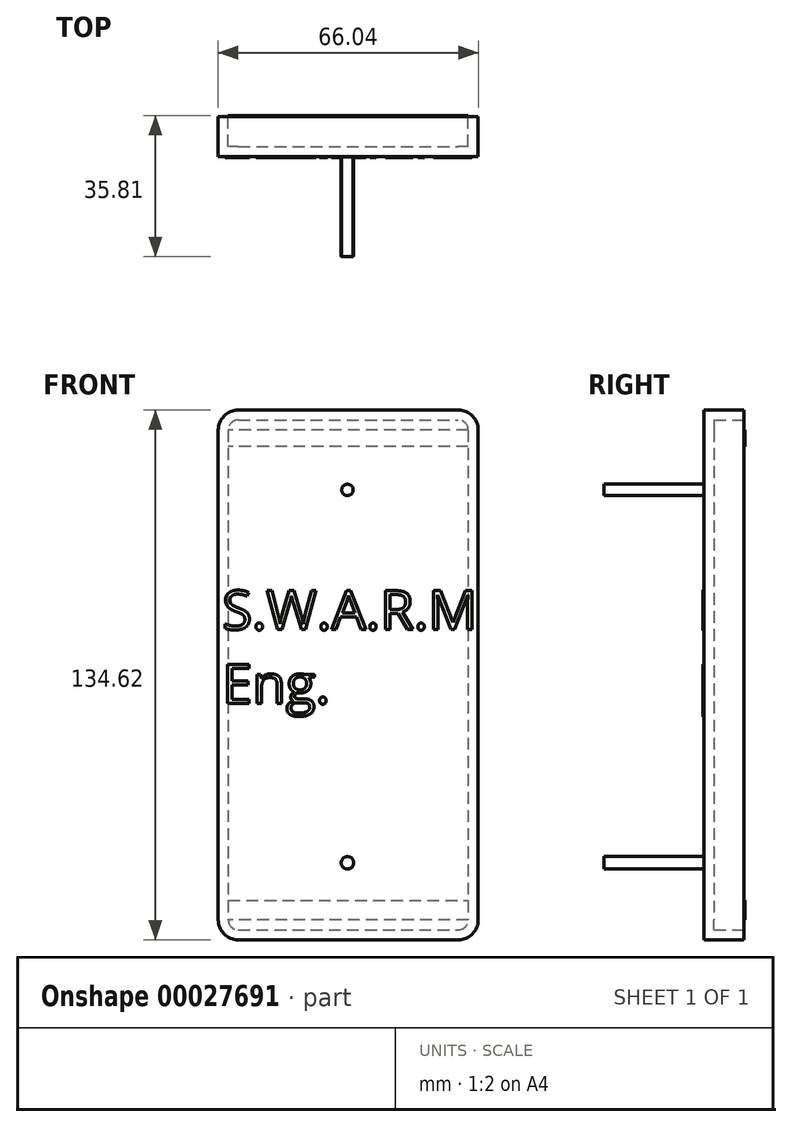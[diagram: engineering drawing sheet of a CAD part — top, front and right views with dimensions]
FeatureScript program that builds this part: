
annotation { "Feature Type Name" : "Feature", "Feature Type Description" : "" }
export const myFeature = defineFeature(function(context is Context, id is Id, definition is map)
    precondition{}
    {
        {
            var Q0;
            Q0=qCreatedBy(makeId("Front.planeOp"),FACE);
            var sketch = newSketch(context, id + "F0", { "sketchPlane" : qUnion([Q0])});
            skLineSegment(sketch, "E0.bottom", {"start": v(-32.82, 79.31) * mm, "end": v(33.22, 79.31) * mm});
            skLineSegment(sketch, "E0.top", {"start": v(-32.82, -55.3) * mm, "end": v(33.22, -55.3) * mm});
            skLineSegment(sketch, "E0.left", {"start": v(-32.82, 79.31) * mm, "end": v(-32.82, -55.3) * mm});
            skLineSegment(sketch, "E0.right", {"start": v(33.22, 79.31) * mm, "end": v(33.22, -55.3) * mm});
            skSolve(sketch);
        }
        {
            var Q0;
            Q0 = qSketchRegion(id + "F0", true);
            extrude(context, id + "F1", {"entities" : qUnion([Q0]), "depth" : 10.16 * mm});
        }
        {
            var Q0;
            Q0=makeQuery(id+"F1.opExtrude","SWEPT_EDGE",EDGE,{"disambiguationData":[OSD([sQuery(id+"F0.wireOp",EDGE,"E0.bottom"),sQuery(id+"F0.wireOp",EDGE,"E0.left")])]});
            var Q1;
            Q1=makeQuery(id+"F1.opExtrude","SWEPT_EDGE",EDGE,{"disambiguationData":[OSD([sQuery(id+"F0.wireOp",EDGE,"E0.bottom"),sQuery(id+"F0.wireOp",EDGE,"E0.right")])]});
            var Q2;
            Q2=makeQuery(id+"F1.opExtrude","SWEPT_EDGE",EDGE,{"disambiguationData":[OSD([sQuery(id+"F0.wireOp",EDGE,"E0.top"),sQuery(id+"F0.wireOp",EDGE,"E0.right")])]});
            var Q3;
            Q3=makeQuery(id+"F1.opExtrude","SWEPT_EDGE",EDGE,{"disambiguationData":[OSD([sQuery(id+"F0.wireOp",EDGE,"E0.top"),sQuery(id+"F0.wireOp",EDGE,"E0.left")])]});
            fillet(context, id + "F2", {"entities" : qUnion([Q0, Q1, Q2, Q3]), "radius" : 5.08 * mm, "tangentPropagation" : true, "allowEdgeOverflow" : false});
        }
        {
            var Q0;
            Q0=makeQuery(id+"F1.opExtrude","CAP_FACE",FACE,{"disambiguationData":[OSD([sQuery(id+"F0.wireOp",EDGE,"E0.bottom"),sQuery(id+"F0.wireOp",EDGE,"E0.top"),sQuery(id+"F0.wireOp",EDGE,"E0.left"),sQuery(id+"F0.wireOp",EDGE,"E0.right")])],"isStart":true});
            shell(context, id + "F3", {"entities" : qUnion([Q0]), "thickness" : 2.54 * mm});
        }
        {
            var Q0;
            Q0=makeQuery(id+"F1.opExtrude","CAP_FACE",FACE,{"disambiguationData":[OSD([sQuery(id+"F0.wireOp",EDGE,"E0.bottom"),sQuery(id+"F0.wireOp",EDGE,"E0.top"),sQuery(id+"F0.wireOp",EDGE,"E0.left"),sQuery(id+"F0.wireOp",EDGE,"E0.right")])],"isStart":true});
            var sketch = newSketch(context, id + "F4", { "sketchPlane" : qUnion([Q0])});
            skLineSegment(sketch, "E1", {"start": v(-30.68, 74.23) * mm, "end": v(30.28, 74.23) * mm});
            skLineSegment(sketch, "E2", {"start": v(-30.68, 74.23) * mm, "end": v(-30.68, 70) * mm});
            skLineSegment(sketch, "E3", {"start": v(-30.68, 70) * mm, "end": v(30.28, 70) * mm});
            skLineSegment(sketch, "E4", {"start": v(30.28, 70) * mm, "end": v(30.28, 74.23) * mm});
            skLineSegment(sketch, "E5", {"start": v(-30.68, -50.23) * mm, "end": v(30.28, -50.23) * mm});
            skLineSegment(sketch, "E6", {"start": v(30.28, -50.23) * mm, "end": v(30.28, -45.31) * mm});
            skLineSegment(sketch, "E7", {"start": v(30.28, -45.31) * mm, "end": v(-30.68, -45.31) * mm});
            skLineSegment(sketch, "E8", {"start": v(-30.68, -45.31) * mm, "end": v(-30.68, -50.23) * mm});
            skSolve(sketch);
        }
        {
            var Q0;
            Q0 = qSketchRegion(id + "F4", true);
            extrude(context, id + "F5", {"entities" : qUnion([Q0]), "depth" : 0.25 * mm});
        }
        {
            var Q0;
            Q0=makeQuery(id+"F1.opExtrude","CAP_FACE",FACE,{"disambiguationData":[OSD([sQuery(id+"F0.wireOp",EDGE,"E0.bottom"),sQuery(id+"F0.wireOp",EDGE,"E0.top"),sQuery(id+"F0.wireOp",EDGE,"E0.left"),sQuery(id+"F0.wireOp",EDGE,"E0.right")])],"isStart":false});
            var sketch = newSketch(context, id + "F6", { "sketchPlane" : qUnion([Q0])});
            skCircle(sketch, "E9", {"center": v(0, 59.02) * mm, "radius": 1.47 * mm});
            skCircle(sketch, "E10", {"center": v(0, -35.72) * mm, "radius": 1.59 * mm});
            skSolve(sketch);
        }
        {
            var Q0;
            Q0 = qSketchRegion(id + "F6", true);
            extrude(context, id + "F7", {"entities" : qUnion([Q0]), "operationType" : NewBodyOperationType.ADD, "depth" : 25.4 * mm});
        }
        {
            var Q0;
            Q0=makeQuery(id+"F1.opExtrude","CAP_FACE",FACE,{"disambiguationData":[OSD([sQuery(id+"F0.wireOp",EDGE,"E0.bottom"),sQuery(id+"F0.wireOp",EDGE,"E0.top"),sQuery(id+"F0.wireOp",EDGE,"E0.left"),sQuery(id+"F0.wireOp",EDGE,"E0.right")])],"isStart":false});
            var sketch = newSketch(context, id + "F8", { "sketchPlane" : qUnion([Q0])});
            skText(sketch, "E11", { "text": "S.W.A.R.M \nEng.", "fontName": "OpenSans-Regular.ttf"});
            const initialGuessF8  = {"E11": [-0.03183, 0.02356, 1, 0, 0.00995]};
            skSetInitialGuess(sketch, initialGuessF8);
            skSolve(sketch);
        }
        {
            var Q0;
            Q0 = qSketchRegion(id + "F8", true);
            extrude(context, id + "F9", {"entities" : qUnion([Q0]), "operationType" : NewBodyOperationType.ADD, "depth" : 0.25 * mm});
        }
    });
